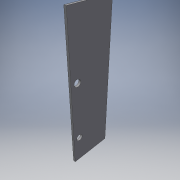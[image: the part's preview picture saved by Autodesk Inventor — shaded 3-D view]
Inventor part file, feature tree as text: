
AUTODESK INVENTOR PART (.ipt)
format: ipt  version: 2016 (Build 200138000, 138)  size: 102,400 bytes
history: native  units: in
note: dims shown in document units (in); Inventor stores cm internally (conversion verified against a paired STEP export)
features: extrude x2, sketch x2
ambient origin geometry x8: Origin, YZ Plane, XZ Plane, XY Plane, X Axis, Y Axis, Z Axis, Center Point
bodies: Solid1 (feature_tree)
feature tree (4):
  extrude  "Extrusion1"  Depth=18.0in
  extrude  "Extrusion2"  Depth=1.0in
  sketch  "Sketch1"  dims[d0=62.0in d1=18.0in]
  sketch  "Sketch2"  dims[d2=1.0in d3=0.0in d5=3.0in d8=2.8in d9=12.0in d10=37.0in d11=2.8in d12=1.0in d13=0.0in]
